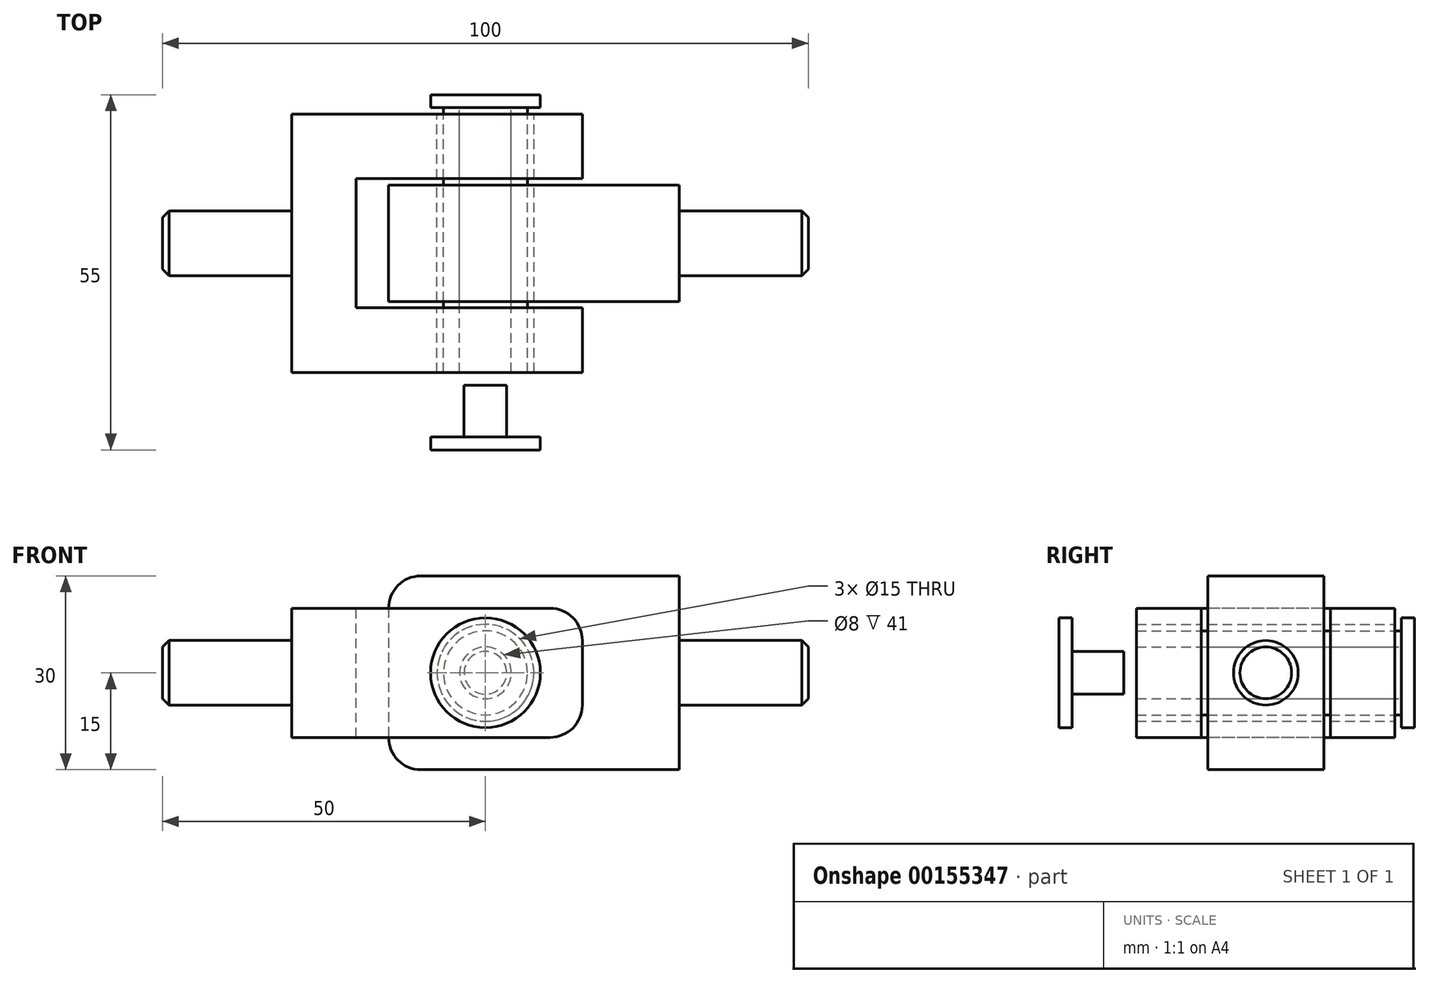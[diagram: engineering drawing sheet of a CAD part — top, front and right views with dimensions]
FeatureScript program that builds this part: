
annotation { "Feature Type Name" : "Feature", "Feature Type Description" : "" }
export const myFeature = defineFeature(function(context is Context, id is Id, definition is map)
    precondition{}
    {
        {
            var Q0;
            Q0=qCreatedBy(makeId("Right.planeOp"),FACE);
            var sketch = newSketch(context, id + "F0", { "sketchPlane" : qUnion([Q0])});
            skLineSegment(sketch, "E0.bottom", {"start": v(0, 0) * mm, "end": v(-40, 0) * mm});
            skLineSegment(sketch, "E0.top", {"start": v(0, -20) * mm, "end": v(-40, -20) * mm});
            skLineSegment(sketch, "E0.left", {"start": v(0, 0) * mm, "end": v(0, -20) * mm});
            skLineSegment(sketch, "E0.right", {"start": v(-40, 0) * mm, "end": v(-40, -20) * mm});
            skCircle(sketch, "E1", {"center": v(-20, -10) * mm, "radius": 5 * mm});
            skSolve(sketch);
        }
        {
            var Q0;
            Q0=makeQuery(id+"F0.imprint","IMPRINT",FACE,{"disambiguationData":[TD([[makeQuery(id+"F0.imprint","IMPRINT",EDGE,{"derivedFrom":sQuery(id+"F0.wireOp",EDGE,"E1")}),1.0]])]});
            extrude(context, id + "F1", {"entities" : qUnion([Q0]), "oppositeDirection" : true, "depth" : 20 * mm});
        }
        {
            var Q0;
            Q0=qCreatedBy(makeId("Top.planeOp"),FACE);
            var sketch = newSketch(context, id + "F2", { "sketchPlane" : qUnion([Q0])});
            skLineSegment(sketch, "E2.bottom", {"start": v(0, 0) * mm, "end": v(45, 0) * mm});
            skLineSegment(sketch, "E2.top", {"start": v(0, -40) * mm, "end": v(45, -40) * mm});
            skLineSegment(sketch, "E2.left", {"start": v(0, 0) * mm, "end": v(0, -40) * mm});
            skLineSegment(sketch, "E2.right", {"start": v(45, 0) * mm, "end": v(45, -40) * mm});
            skLineSegment(sketch, "E3.bottom", {"start": v(45, -10) * mm, "end": v(10, -10) * mm});
            skLineSegment(sketch, "E3.top", {"start": v(45, -30) * mm, "end": v(10, -30) * mm});
            skLineSegment(sketch, "E3.left", {"start": v(45, -10) * mm, "end": v(45, -30) * mm});
            skLineSegment(sketch, "E3.right", {"start": v(10, -10) * mm, "end": v(10, -30) * mm});
            skPoint(sketch, "E4.startSnap0", {"position": v(22.5, 0) * mm});
            skPoint(sketch, "E4.endSnap0", {"position": v(27.5, -10) * mm});
            skLineSegment(sketch, "E5", {"start": v(15, -10) * mm, "end": v(15, -30) * mm});
            skLineSegment(sketch, "E6", {"start": v(15, -30) * mm, "end": v(60, -30) * mm});
            skLineSegment(sketch, "E7", {"start": v(60, -30) * mm, "end": v(60, -10) * mm});
            skLineSegment(sketch, "E8", {"start": v(60, -10) * mm, "end": v(15, -10) * mm});
            skLineSegment(sketch, "E9", {"start": v(64.5, 2) * mm, "end": v(-13.4, 2) * mm});
            skSolve(sketch);
        }
        {
            var Q0;
            {var subQ0=sQuery(id+"F2.wireOp",EDGE,"E2.left");Q0=makeQuery(id+"F2.imprint","IMPRINT",FACE,{"disambiguationData":[TD([[makeQuery(id+"F2.imprint","IMPRINT",EDGE,{"derivedFrom":subQ0}),1.0]])]});}
            var Q1;
            {var subQ0=sQuery(id+"F2.wireOp",EDGE,"lwf0jP7u-qRGJ-sjRD-eBDz-npzYwXVrge2I");var subQ1=sQuery(id+"F2.wireOp",EDGE,"E2.bottom");var subQ2=makeQuery(id+"F2.imprint","INTERSECT",VERTEX,{"derivedFrom":[subQ1,subQ0]});Q1=makeQuery(id+"F2.imprint","IMPRINT",FACE,{"disambiguationData":[TD([[makeQuery(id+"F2.imprint","IMPRINT",EDGE,{"disambiguationData":[TD([[subQ2,1.0]])],"derivedFrom":subQ1}),-1.0]])]});}
            var Q2;
            {var subQ0=sQuery(id+"F2.wireOp",EDGE,"E2.right");var subQ1=sQuery(id+"F2.wireOp",EDGE,"E2.bottom");var subQ2=makeQuery(id+"F2.imprint","INTERSECT",VERTEX,{"derivedFrom":[subQ1,subQ0]});Q2=makeQuery(id+"F2.imprint","IMPRINT",FACE,{"disambiguationData":[TD([[makeQuery(id+"F2.imprint","IMPRINT",EDGE,{"disambiguationData":[TD([[subQ2,1.0]])],"derivedFrom":subQ1}),-1.0]])]});}
            var Q3;
            {var subQ0=sQuery(id+"F2.wireOp",EDGE,"E2.right");var subQ1=sQuery(id+"F2.wireOp",EDGE,"E2.top");var subQ2=makeQuery(id+"F2.imprint","INTERSECT",VERTEX,{"derivedFrom":[subQ1,subQ0]});Q3=makeQuery(id+"F2.imprint","IMPRINT",FACE,{"disambiguationData":[TD([[makeQuery(id+"F2.imprint","IMPRINT",EDGE,{"disambiguationData":[TD([[subQ2,1.0]])],"derivedFrom":subQ1}),1.0]])]});}
            var Q4;
            {var subQ0=sQuery(id+"F2.wireOp",EDGE,"lwf0jP7u-qRGJ-sjRD-eBDz-npzYwXVrge2I");var subQ1=sQuery(id+"F2.wireOp",EDGE,"E2.top");var subQ2=makeQuery(id+"F2.imprint","INTERSECT",VERTEX,{"derivedFrom":[subQ1,subQ0]});Q4=makeQuery(id+"F2.imprint","IMPRINT",FACE,{"disambiguationData":[TD([[makeQuery(id+"F2.imprint","IMPRINT",EDGE,{"disambiguationData":[TD([[subQ2,1.0]])],"derivedFrom":subQ1}),1.0]])]});}
            extrude(context, id + "F3", {"entities" : qUnion([Q0, Q1, Q2, Q3, Q4]), "oppositeDirection" : true, "depth" : 20 * mm});
        }
        {
            var Q0;
            {var subQ0=sQuery(id+"F2.wireOp",EDGE,"E2.right");Q0=makeQuery(id+"F3.opExtrude","CAP_EDGE",EDGE,{"disambiguationData":[OSD([subQ0]),TDD([makeQuery(id+"F2.imprint","IMPRINT",EDGE,{"disambiguationData":[TD([[makeQuery(id+"F2.imprint","INTERSECT",VERTEX,{"derivedFrom":[sQuery(id+"F2.wireOp",EDGE,"E2.top"),subQ0]}),1.0]])],"derivedFrom":subQ0})])],"isStart":true});}
            var Q1;
            {var subQ0=sQuery(id+"F2.wireOp",EDGE,"E2.right");Q1=makeQuery(id+"F3.opExtrude","CAP_EDGE",EDGE,{"disambiguationData":[OSD([subQ0]),TDD([makeQuery(id+"F2.imprint","IMPRINT",EDGE,{"disambiguationData":[TD([[makeQuery(id+"F2.imprint","INTERSECT",VERTEX,{"derivedFrom":[sQuery(id+"F2.wireOp",EDGE,"E2.bottom"),subQ0]}),-1.0]])],"derivedFrom":subQ0})])],"isStart":true});}
            var Q2;
            {var subQ0=sQuery(id+"F2.wireOp",EDGE,"E2.right");Q2=makeQuery(id+"F3.opExtrude","CAP_EDGE",EDGE,{"disambiguationData":[OSD([subQ0]),TDD([makeQuery(id+"F2.imprint","IMPRINT",EDGE,{"disambiguationData":[TD([[makeQuery(id+"F2.imprint","INTERSECT",VERTEX,{"derivedFrom":[sQuery(id+"F2.wireOp",EDGE,"E2.top"),subQ0]}),1.0]])],"derivedFrom":subQ0})])],"isStart":false});}
            var Q3;
            {var subQ0=sQuery(id+"F2.wireOp",EDGE,"E2.right");Q3=makeQuery(id+"F3.opExtrude","CAP_EDGE",EDGE,{"disambiguationData":[OSD([subQ0]),TDD([makeQuery(id+"F2.imprint","IMPRINT",EDGE,{"disambiguationData":[TD([[makeQuery(id+"F2.imprint","INTERSECT",VERTEX,{"derivedFrom":[sQuery(id+"F2.wireOp",EDGE,"E2.bottom"),subQ0]}),-1.0]])],"derivedFrom":subQ0})])],"isStart":false});}
            fillet(context, id + "F4", {"entities" : qUnion([Q0, Q1, Q2, Q3]), "radius" : 5 * mm, "tangentPropagation" : true, "allowEdgeOverflow" : false});
        }
        {
            var Q0;
            Q0=qCreatedBy(makeId("Front.planeOp"),FACE);
            var sketch = newSketch(context, id + "F5", { "sketchPlane" : qUnion([Q0])});
            skCircle(sketch, "E10", {"center": v(30, -10) * mm, "radius": 7.5 * mm});
            skLineSegment(sketch, "E11", {"start": v(15, 5) * mm, "end": v(15, -25) * mm});
            skLineSegment(sketch, "E12", {"start": v(15, -25) * mm, "end": v(60, -25) * mm});
            skLineSegment(sketch, "E13", {"start": v(60, -25) * mm, "end": v(60, 5) * mm});
            skLineSegment(sketch, "E14", {"start": v(60, 5) * mm, "end": v(15, 5) * mm});
            skLineSegment(sketch, "E15", {"start": v(60, -5) * mm, "end": v(80, -5) * mm});
            skLineSegment(sketch, "E16", {"start": v(80, -5) * mm, "end": v(80, -15) * mm});
            skLineSegment(sketch, "E17", {"start": v(80, -15) * mm, "end": v(60, -15) * mm});
            skCircle(sketch, "E18", {"center": v(30, -10) * mm, "radius": 6.5 * mm});
            skCircle(sketch, "E19", {"center": v(30, -10) * mm, "radius": 4 * mm});
            skCircle(sketch, "E20", {"center": v(30, -10) * mm, "radius": 3.3 * mm});
            skSolve(sketch);
        }
        {
            var Q0;
            Q0=sQuery(id+"F5.wireOp",VERTEX,"E10.center");
            var Q1;
            Q1=makeQuery(id+"F3.opExtrude","SWEPT_BODY",BODY,{"disambiguationData":[OSD([sQuery(id+"F2.wireOp",EDGE,"E2.bottom"),sQuery(id+"F2.wireOp",EDGE,"E2.top"),sQuery(id+"F2.wireOp",EDGE,"E2.left"),sQuery(id+"F2.wireOp",EDGE,"E2.right"),sQuery(id+"F2.wireOp",EDGE,"E3.bottom"),sQuery(id+"F2.wireOp",EDGE,"E3.top"),sQuery(id+"F2.wireOp",EDGE,"E3.right")])]});
            hole(context, id + "F6", {"style" : HoleStyle.SIMPLE, "endStyle" : HoleEndStyle.THROUGH, "oppositeDirection" : true, "holeDiameter" : 15 * mm, "locations" : qUnion([Q0]), "scope" : qUnion([Q1]), "isTappedThrough" : true});
        }
        {
            var Q0;
            Q0=makeQuery(id+"F1.opExtrude","CAP_FACE",FACE,{"disambiguationData":[OSD([sQuery(id+"F0.wireOp",EDGE,"E1")])],"isStart":false});
            chamfer(context, id + "F7", {"entities" : qUnion([Q0]), "width" : 1 * mm, "tangentPropagation" : true});
        }
        {
            var Q0;
            Q0=makeQuery(id+"F5.imprint","IMPRINT",FACE,{"disambiguationData":[TD([[makeQuery(id+"F5.imprint","IMPRINT",EDGE,{"derivedFrom":sQuery(id+"F5.wireOp",EDGE,"E18")}),1.0]])]});
            var Q1;
            Q1=makeQuery(id+"F3.opExtrude","SWEPT_FACE",FACE,{"disambiguationData":[OSD([sQuery(id+"F2.wireOp",EDGE,"E2.top")])]});
            extrude(context, id + "F8", {"entities" : qUnion([Q0]), "operationType" : NewBodyOperationType.ADD, "endBoundEntityFace" : qUnion([Q1]), "depth" : 40 * mm, "hasSecondDirection" : true, "secondDirectionOppositeDirection" : true, "secondDirectionDepth" : 1 * mm});
        }
        {
            var Q0;
            Q0=makeQuery(id+"F5.imprint","IMPRINT",FACE,{"disambiguationData":[TD([[makeQuery(id+"F5.imprint","IMPRINT",EDGE,{"derivedFrom":sQuery(id+"F5.wireOp",EDGE,"E10")}),-1.0]])]});
            extrude(context, id + "F9", {"entities" : qUnion([Q0]), "operationType" : NewBodyOperationType.ADD, "depth" : 29 * mm, "hasSecondDirection" : true, "secondDirectionOppositeDirection" : false, "secondDirectionDepth" : 11 * mm});
        }
        {
            var Q0;
            Q0=makeQuery(id+"F9.opExtrude","SWEPT_EDGE",EDGE,{"disambiguationData":[OSD([sQuery(id+"F5.wireOp",EDGE,"E11"),sQuery(id+"F5.wireOp",EDGE,"E14")])]});
            var Q1;
            Q1=makeQuery(id+"F9.opExtrude","SWEPT_EDGE",EDGE,{"disambiguationData":[OSD([sQuery(id+"F5.wireOp",EDGE,"E11"),sQuery(id+"F5.wireOp",EDGE,"E12")])]});
            fillet(context, id + "F10", {"entities" : qUnion([Q0, Q1]), "radius" : 5 * mm, "tangentPropagation" : true, "allowEdgeOverflow" : false});
        }
        {
            var Q0;
            {var subQ0=sQuery(id+"F5.wireOp",EDGE,"E15");Q0=makeQuery(id+"F5.imprint","IMPRINT",FACE,{"disambiguationData":[TD([[makeQuery(id+"F5.imprint","IMPRINT",EDGE,{"derivedFrom":subQ0}),-1.0]])]});}
            extrude(context, id + "F11", {"entities" : qUnion([Q0]), "operationType" : NewBodyOperationType.ADD, "depth" : 25 * mm, "hasSecondDirection" : true, "secondDirectionOppositeDirection" : false, "secondDirectionDepth" : 15 * mm});
        }
        {
            var Q0;
            Q0=makeQuery(id+"F11.opExtrude","CAP_EDGE",EDGE,{"disambiguationData":[OSD([sQuery(id+"F5.wireOp",EDGE,"E15")])],"isStart":false});
            var Q1;
            Q1=makeQuery(id+"F11.opExtrude","CAP_EDGE",EDGE,{"disambiguationData":[OSD([sQuery(id+"F5.wireOp",EDGE,"E15")])],"isStart":true});
            var Q2;
            Q2=makeQuery(id+"F11.opExtrude","CAP_EDGE",EDGE,{"disambiguationData":[OSD([sQuery(id+"F5.wireOp",EDGE,"E17")])],"isStart":true});
            var Q3;
            Q3=makeQuery(id+"F11.opExtrude","CAP_EDGE",EDGE,{"disambiguationData":[OSD([sQuery(id+"F5.wireOp",EDGE,"E17")])],"isStart":false});
            fillet(context, id + "F12", {"entities" : qUnion([Q0, Q1, Q2, Q3]), "radius" : 5 * mm, "tangentPropagation" : true, "allowEdgeOverflow" : false});
        }
        {
            var Q0;
            Q0=makeQuery(id+"F11.opExtrude","SWEPT_FACE",FACE,{"disambiguationData":[OSD([sQuery(id+"F5.wireOp",EDGE,"E16")])]});
            chamfer(context, id + "F13", {"entities" : qUnion([Q0]), "width" : 1 * mm, "tangentPropagation" : true});
        }
        {
            var Q0;
            Q0=qCreatedBy(makeId("Front.planeOp"),FACE);
            var sketch = newSketch(context, id + "F14", { "sketchPlane" : qUnion([Q0])});
            skCircle(sketch, "E21", {"center": v(30, -10) * mm, "radius": 8.5 * mm});
            skSolve(sketch);
        }
        {
            var Q0;
            Q0=makeQuery(id+"F14.imprint","IMPRINT",FACE,{"disambiguationData":[TD([[makeQuery(id+"F14.imprint","IMPRINT",EDGE,{"derivedFrom":sQuery(id+"F14.wireOp",EDGE,"E21")}),1.0]])]});
            extrude(context, id + "F15", {"entities" : qUnion([Q0]), "operationType" : NewBodyOperationType.ADD, "oppositeDirection" : true, "depth" : 3 * mm, "hasSecondDirection" : true, "secondDirectionOppositeDirection" : true, "secondDirectionDepth" : 1 * mm});
        }
        {
            var Q0;
            Q0=makeQuery(id+"F14.imprint","IMPRINT",FACE,{"disambiguationData":[TD([[makeQuery(id+"F14.imprint","IMPRINT",EDGE,{"derivedFrom":sQuery(id+"F14.wireOp",EDGE,"E21")}),1.0]])]});
            extrude(context, id + "F16", {"entities" : qUnion([Q0]), "oppositeDirection" : true, "depth" : 10 * mm, "hasSecondDirection" : true, "secondDirectionOppositeDirection" : true, "secondDirectionDepth" : 8 * mm});
        }
        {
            var Q0;
            Q0=makeQuery(id+"F16.opExtrude","SWEPT_BODY",BODY,{"disambiguationData":[OSD([sQuery(id+"F14.wireOp",EDGE,"E21")])]});
            var Q1;
            Q1=qCreatedBy(makeId("Front.planeOp"),FACE);
            transform(context, id + "F17", {"entities" : qUnion([Q0]), "transformType" : TransformType.TRANSLATION_DISTANCE, "transformDirection" : qUnion([Q1]), "distance" : 60 * mm, "makeCopy" : false});
        }
        {
            var Q0;
            Q0=makeQuery(id+"F5.imprint","IMPRINT",FACE,{"disambiguationData":[TD([[makeQuery(id+"F5.imprint","IMPRINT",EDGE,{"derivedFrom":sQuery(id+"F5.wireOp",EDGE,"E19")}),1.0]])]});
            var Q1;
            Q1=makeQuery(id+"F5.imprint","IMPRINT",FACE,{"disambiguationData":[TD([[makeQuery(id+"F5.imprint","IMPRINT",EDGE,{"derivedFrom":sQuery(id+"F5.wireOp",EDGE,"E20")}),1.0]])]});
            extrude(context, id + "F18", {"entities" : qUnion([Q0, Q1]), "depth" : 30 * mm});
        }
        {
            var Q0;
            Q0=makeQuery(id+"F5.imprint","IMPRINT",FACE,{"disambiguationData":[TD([[makeQuery(id+"F5.imprint","IMPRINT",EDGE,{"derivedFrom":sQuery(id+"F5.wireOp",EDGE,"E20")}),1.0]])]});
            extrude(context, id + "F19", {"entities" : qUnion([Q0]), "operationType" : NewBodyOperationType.ADD, "depth" : 50 * mm, "hasSecondDirection" : true, "secondDirectionOppositeDirection" : false, "secondDirectionDepth" : 42 * mm});
        }
    });
